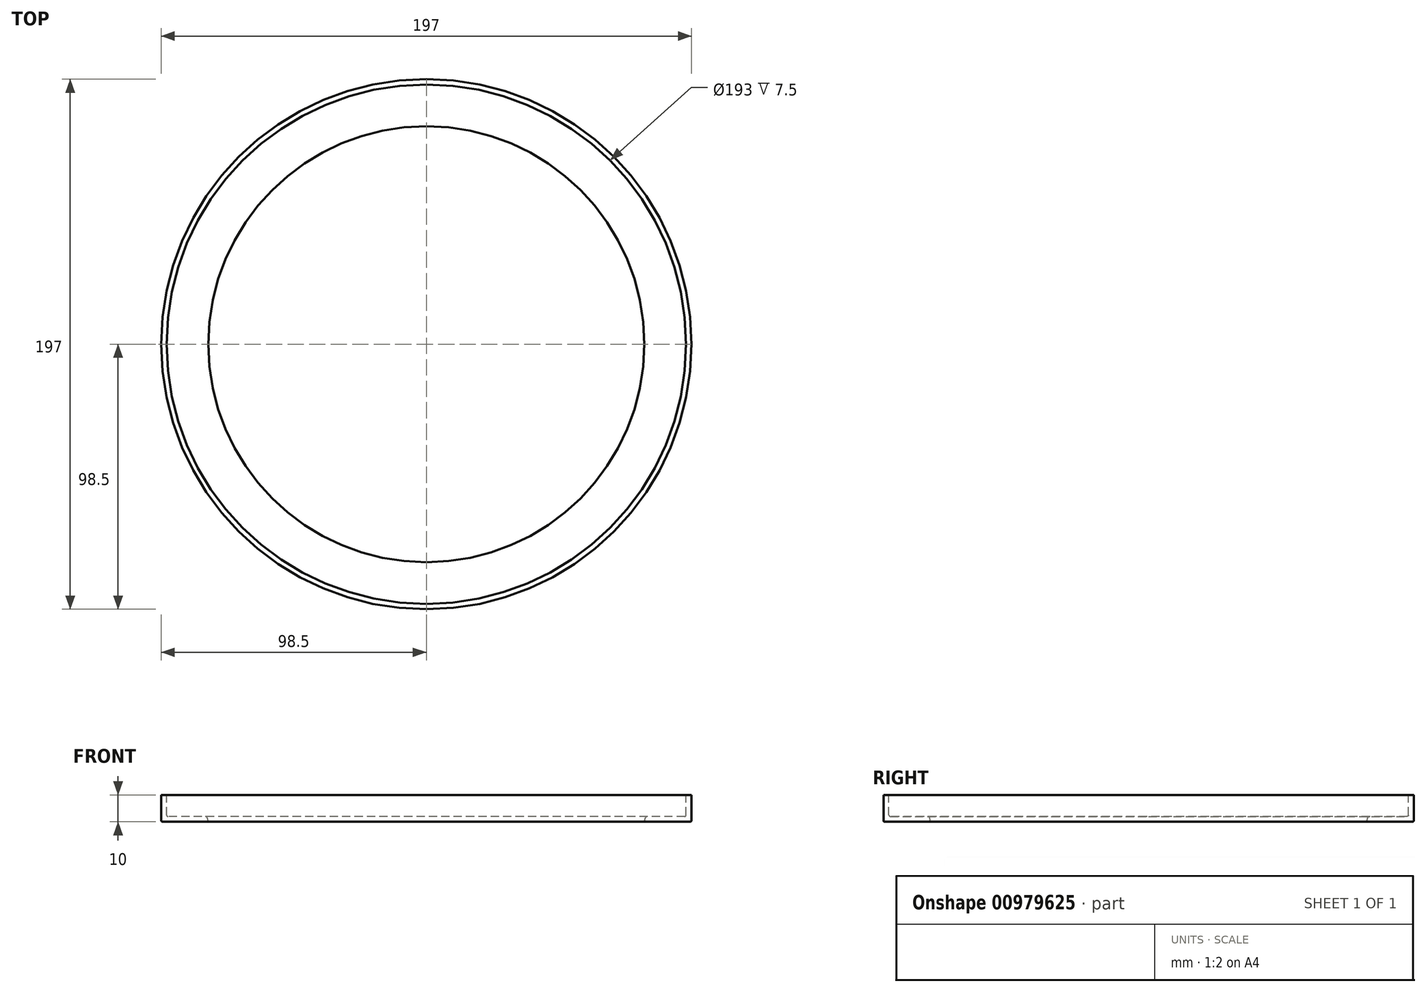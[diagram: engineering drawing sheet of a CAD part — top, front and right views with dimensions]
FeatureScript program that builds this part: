
annotation { "Feature Type Name" : "Feature", "Feature Type Description" : "" }
export const myFeature = defineFeature(function(context is Context, id is Id, definition is map)
    precondition{}
    {
        {
            var Q0;
            Q0=qCreatedBy(makeId("Front.planeOp"),FACE);
            var sketch = newSketch(context, id + "F0", { "sketchPlane" : qUnion([Q0]), "disableImprinting" : false});
            skLineSegment(sketch, "E0", {"start": v(96.5, 10) * mm, "end": v(96.5, 2.5) * mm});
            skLineSegment(sketch, "E1", {"start": v(96, 2) * mm, "end": v(82.12, 2) * mm});
            skLineSegment(sketch, "E2", {"start": v(81.35, 1.4) * mm, "end": v(81, 0) * mm});
            skLineSegment(sketch, "E3", {"start": v(96.5, 10) * mm, "end": v(98.5, 10) * mm});
            skLineSegment(sketch, "E4", {"start": v(98.5, 10) * mm, "end": v(98.5, 0.5) * mm});
            skLineSegment(sketch, "E5", {"start": v(98, 0) * mm, "end": v(81, 0) * mm});
            skLineSegment(sketch, "E6", {"start": v(0, 42.82) * mm, "end": v(0, -41.43) * mm, "construction": true});
            skPoint(sketch, "E7.visualSharp", {"position": v(81.5, 2) * mm});
            skArc(sketch, "E7.filletArc", {"start": v(82.12, 2) * mm, "mid": v(81.63, 1.83) * mm, "end": v(81.35, 1.4) * mm});
            skPoint(sketch, "E8.0.visualSharp", {"position": v(96.5, 2) * mm});
            skArc(sketch, "E8.0.filletArc", {"start": v(96, 2) * mm, "mid": v(96.35, 2.15) * mm, "end": v(96.5, 2.5) * mm});
            skPoint(sketch, "E9.0.visualSharp", {"position": v(98.5, 0) * mm});
            skArc(sketch, "E9.0.filletArc", {"start": v(98, 0) * mm, "mid": v(98.35, 0.15) * mm, "end": v(98.5, 0.5) * mm});
            skSolve(sketch);
        }
        {
            var Q0;
            Q0 = qSketchRegion(id + "F0", true);
            var Q1;
            Q1=sQuery(id+"F0.wireOp",EDGE,"E6");
            revolve(context, id + "F1", {"surfaceOperationType" : NewSurfaceOperationType.NEW, "entities" : qUnion([Q0]), "axis" : qUnion([Q1]), "revolveType" : RevolveType.FULL});
        }
    });
